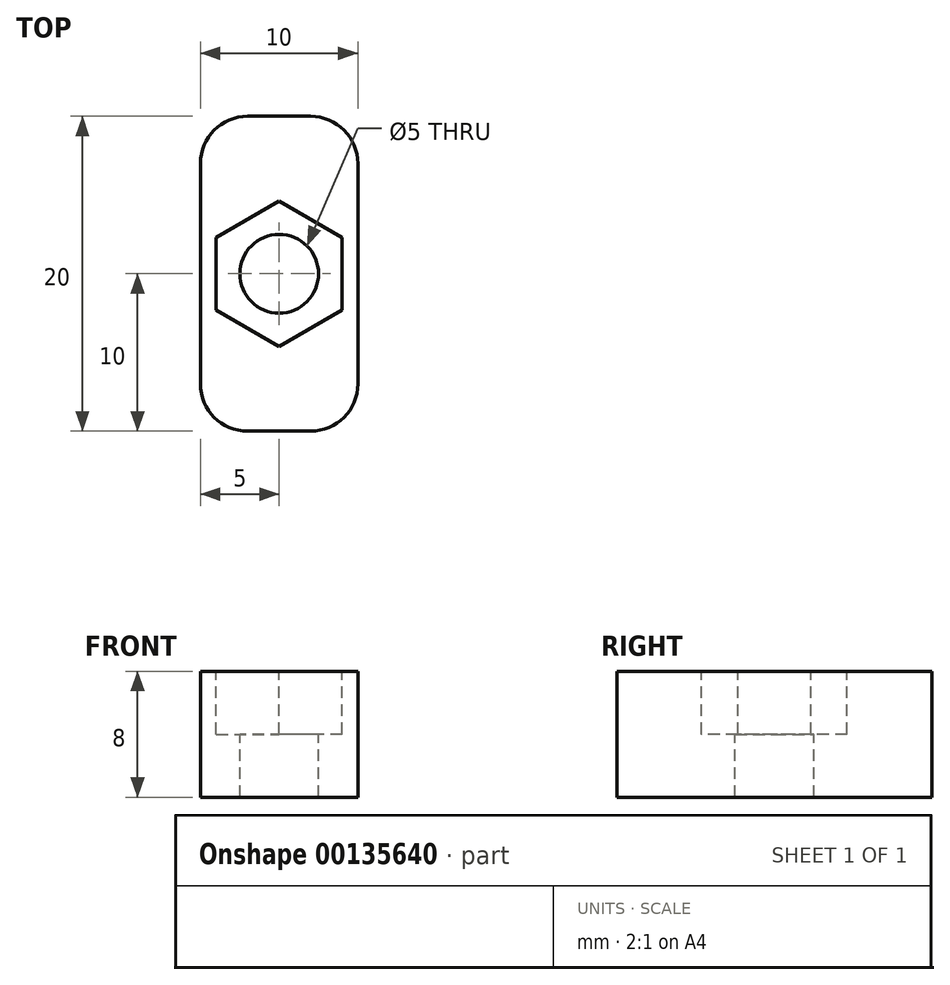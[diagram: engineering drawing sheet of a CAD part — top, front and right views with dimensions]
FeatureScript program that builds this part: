
annotation { "Feature Type Name" : "Feature", "Feature Type Description" : "" }
export const myFeature = defineFeature(function(context is Context, id is Id, definition is map)
    precondition{}
    {
        {
            var Q0;
            Q0=qCreatedBy(makeId("Top.planeOp"),FACE);
            var sketch = newSketch(context, id + "F0", { "sketchPlane" : qUnion([Q0])});
            skLineSegment(sketch, "E0.bottom", {"start": v(2, -10) * mm, "end": v(-2, -10) * mm});
            skLineSegment(sketch, "E0.top", {"start": v(2, 10) * mm, "end": v(-2, 10) * mm});
            skLineSegment(sketch, "E0.left", {"start": v(5, -7) * mm, "end": v(5, 7) * mm});
            skLineSegment(sketch, "E0.right", {"start": v(-5, -7) * mm, "end": v(-5, 7) * mm});
            skPoint(sketch, "E0.middle", {"position": v(0, 0) * mm});
            skPoint(sketch, "E1.visualSharp", {"position": v(-5, 10) * mm});
            skArc(sketch, "E1.filletArc", {"start": v(-2, 10) * mm, "mid": v(-4.12, 9.12) * mm, "end": v(-5, 7) * mm});
            skPoint(sketch, "E2.visualSharp", {"position": v(5, 10) * mm});
            skArc(sketch, "E2.filletArc", {"start": v(5, 7) * mm, "mid": v(4.12, 9.12) * mm, "end": v(2, 10) * mm});
            skPoint(sketch, "E3.visualSharp", {"position": v(5, -10) * mm});
            skArc(sketch, "E3.filletArc", {"start": v(2, -10) * mm, "mid": v(4.12, -9.12) * mm, "end": v(5, -7) * mm});
            skPoint(sketch, "E4.visualSharp", {"position": v(-5, -10) * mm});
            skArc(sketch, "E4.filletArc", {"start": v(-5, -7) * mm, "mid": v(-4.12, -9.12) * mm, "end": v(-2, -10) * mm});
            skSolve(sketch);
        }
        {
            var Q0;
            Q0 = qSketchRegion(id + "F0", true);
            extrude(context, id + "F1", {"entities" : qUnion([Q0]), "depth" : 8 * mm});
        }
        {
            var Q0;
            Q0=makeQuery(id+"F1.opExtrude","CAP_FACE",FACE,{"disambiguationData":[OSD([sQuery(id+"F0.wireOp",EDGE,"E0.bottom"),sQuery(id+"F0.wireOp",EDGE,"E0.top"),sQuery(id+"F0.wireOp",EDGE,"E0.left"),sQuery(id+"F0.wireOp",EDGE,"E0.right")])],"isStart":false});
            var sketch = newSketch(context, id + "F2", { "sketchPlane" : qUnion([Q0])});
            skCircle(sketch, "E5", {"center": v(0, 0) * mm, "radius": 2.5 * mm});
            skSolve(sketch);
        }
        {
            var Q0;
            Q0 = qSketchRegion(id + "F2", true);
            extrude(context, id + "F3", {"entities" : qUnion([Q0]), "operationType" : NewBodyOperationType.REMOVE, "oppositeDirection" : true, "depth" : 25 * mm});
        }
        {
            var Q0;
            Q0=makeQuery(id+"F1.opExtrude","CAP_FACE",FACE,{"disambiguationData":[OSD([sQuery(id+"F0.wireOp",EDGE,"E0.bottom"),sQuery(id+"F0.wireOp",EDGE,"E0.top"),sQuery(id+"F0.wireOp",EDGE,"E0.left"),sQuery(id+"F0.wireOp",EDGE,"E0.right")])],"isStart":false});
            var sketch = newSketch(context, id + "F4", { "sketchPlane" : qUnion([Q0])});
            skCircle(sketch, "E6.cCircle", {"center": v(0, 0) * mm, "radius": 4 * mm, "construction": true});
            skLineSegment(sketch, "E6.0", {"start": v(4, -2.3) * mm, "end": v(0, -4.62) * mm});
            skLineSegment(sketch, "E6.1", {"start": v(0, -4.62) * mm, "end": v(-4, -2.3) * mm});
            skLineSegment(sketch, "E6.2", {"start": v(-4, -2.3) * mm, "end": v(-4, 2.3) * mm});
            skLineSegment(sketch, "E6.3", {"start": v(-4, 2.3) * mm, "end": v(0, 4.62) * mm});
            skLineSegment(sketch, "E6.4", {"start": v(0, 4.62) * mm, "end": v(4, 2.3) * mm});
            skLineSegment(sketch, "E6.5", {"start": v(4, 2.3) * mm, "end": v(4, -2.3) * mm});
            skPoint(sketch, "E6.0.midPoint", {"position": v(2, -3.46) * mm});
            skSolve(sketch);
        }
        {
            var Q0;
            Q0 = qSketchRegion(id + "F4", true);
            extrude(context, id + "F5", {"entities" : qUnion([Q0]), "operationType" : NewBodyOperationType.REMOVE, "oppositeDirection" : true, "depth" : 4 * mm});
        }
    });
